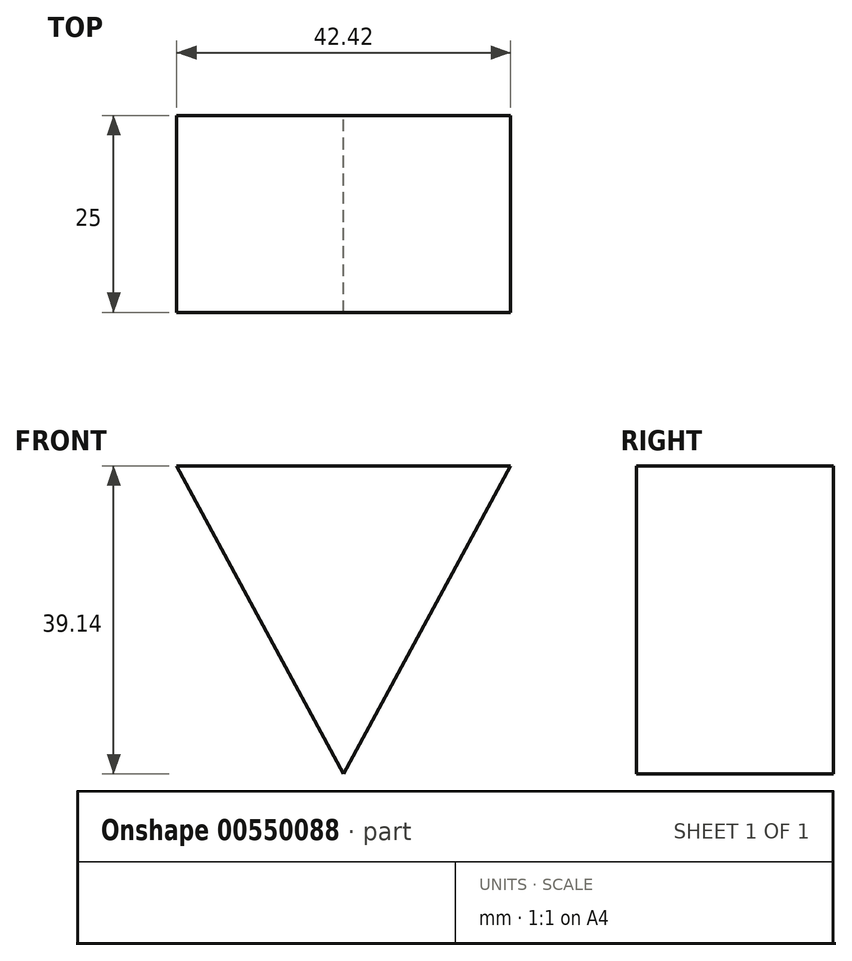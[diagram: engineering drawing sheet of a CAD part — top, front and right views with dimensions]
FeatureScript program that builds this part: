
annotation { "Feature Type Name" : "Feature", "Feature Type Description" : "" }
export const myFeature = defineFeature(function(context is Context, id is Id, definition is map)
    precondition{}
    {
        {
            var Q0;
            Q0=qCreatedBy(makeId("Front.planeOp"),FACE);
            var sketch = newSketch(context, id + "F0", { "sketchPlane" : qUnion([Q0])});
            skLineSegment(sketch, "E0", {"start": v(0, 39.14) * mm, "end": v(-21.2, 39.14) * mm});
            skLineSegment(sketch, "E1", {"start": v(-21.2, 39.14) * mm, "end": v(0, 0) * mm});
            skLineSegment(sketch, "E2.MirrorCS", {"start": v(0, 39.14) * mm, "end": v(21.2, 39.14) * mm});
            skLineSegment(sketch, "E3.MirrorCS", {"start": v(21.2, 39.14) * mm, "end": v(0, 0) * mm});
            skLineSegment(sketch, "E4", {"start": v(0, 59.04) * mm, "end": v(0, 0) * mm});
            skSolve(sketch);
        }
        {
            var Q0;
            {var subQ0=sQuery(id+"F0.wireOp",EDGE,"E0");Q0=makeQuery(id+"F0.imprint","IMPRINT",FACE,{"disambiguationData":[TD([[makeQuery(id+"F0.imprint","IMPRINT",EDGE,{"derivedFrom":subQ0}),1.0]])]});}
            var Q1;
            {var subQ0=sQuery(id+"F0.wireOp",EDGE,"E2.MirrorCS");Q1=makeQuery(id+"F0.imprint","IMPRINT",FACE,{"disambiguationData":[TD([[makeQuery(id+"F0.imprint","IMPRINT",EDGE,{"derivedFrom":subQ0}),-1.0]])]});}
            var Q2;
            Q2=sQuery(id+"F0.wireOp",EDGE,"E1");
            var Q3;
            Q3=sQuery(id+"F0.wireOp",EDGE,"E3.MirrorCS");
            var Q4;
            Q4=sQuery(id+"F0.wireOp",EDGE,"E2.MirrorCS");
            var Q5;
            Q5=sQuery(id+"F0.wireOp",EDGE,"E0");
            var Q6;
            Q6=sQuery(id+"F0.wireOp",EDGE,"E4");
            extrude(context, id + "F1", {"entities" : qUnion([Q0, Q1]), "surfaceEntities" : qUnion([Q2, Q3, Q4, Q5, Q6]), "depth" : 25 * mm, "offsetDistance" : 25 * mm});
        }
    });
